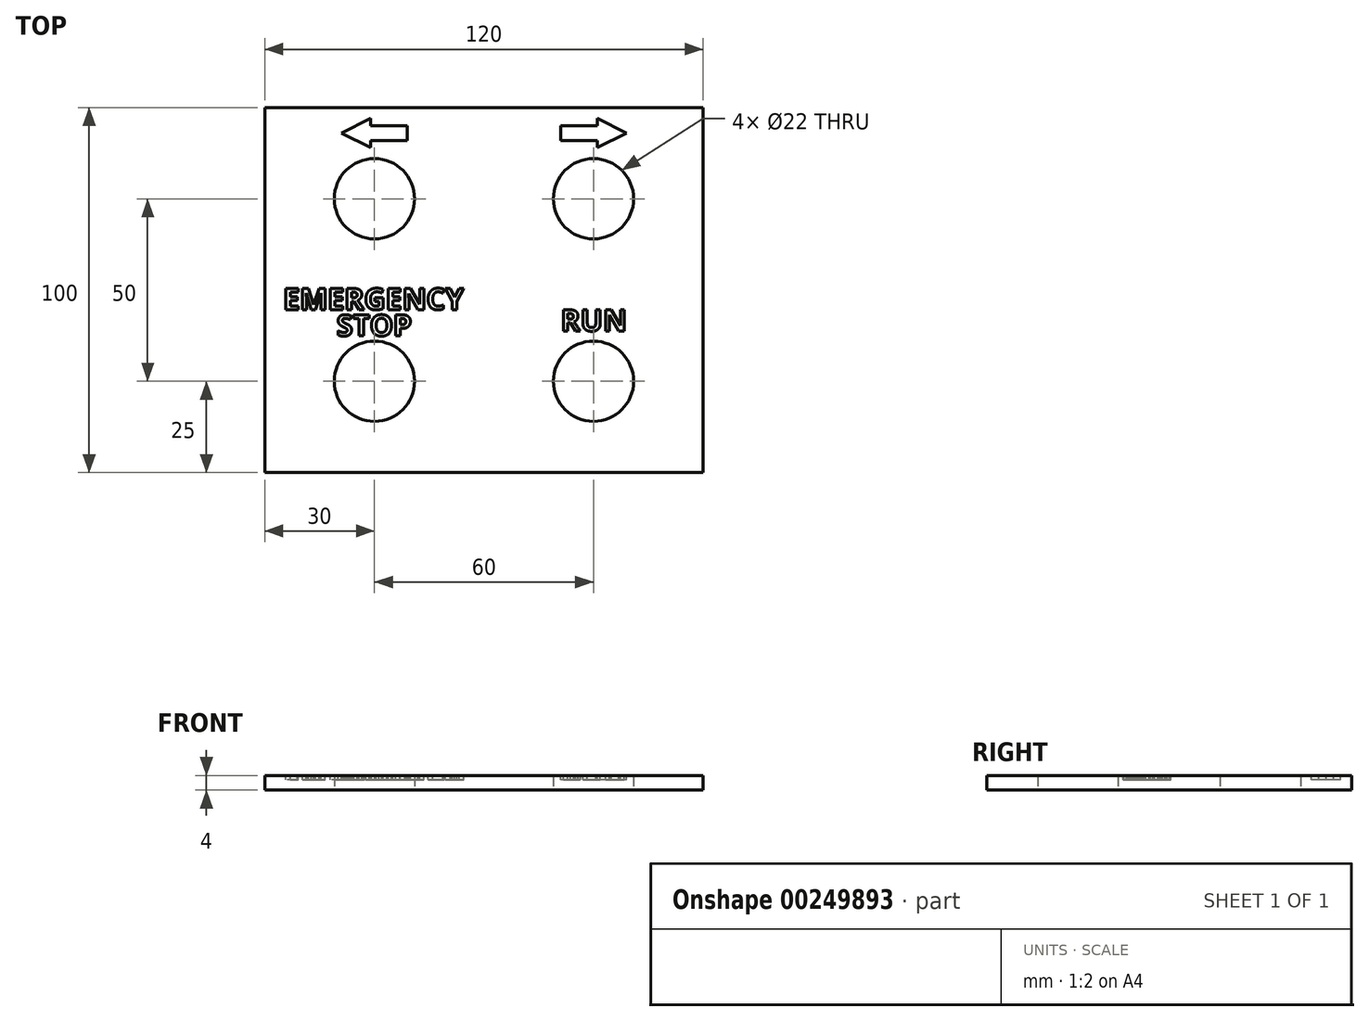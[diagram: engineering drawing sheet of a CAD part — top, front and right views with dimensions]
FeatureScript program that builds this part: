
annotation { "Feature Type Name" : "Feature", "Feature Type Description" : "" }
export const myFeature = defineFeature(function(context is Context, id is Id, definition is map)
    precondition{}
    {
        {
            var Q0;
            Q0=qCreatedBy(makeId("Top.planeOp"),FACE);
            var sketch = newSketch(context, id + "F0", { "sketchPlane" : qUnion([Q0])});
            skLineSegment(sketch, "E0.bottom", {"start": v(60, -50) * mm, "end": v(-60, -50) * mm});
            skLineSegment(sketch, "E0.top", {"start": v(60, 50) * mm, "end": v(-60, 50) * mm});
            skLineSegment(sketch, "E0.left", {"start": v(60, -50) * mm, "end": v(60, 50) * mm});
            skLineSegment(sketch, "E0.right", {"start": v(-60, -50) * mm, "end": v(-60, 50) * mm});
            skPoint(sketch, "E0.middle", {"position": v(0, 0) * mm});
            skCircle(sketch, "E1", {"center": v(-30, 25) * mm, "radius": 11 * mm});
            skLineSegment(sketch, "E2", {"start": v(0, -50) * mm, "end": v(0, 50) * mm, "construction": true});
            skLineSegment(sketch, "E3", {"start": v(-60, 0) * mm, "end": v(60, 0) * mm, "construction": true});
            skCircle(sketch, "E4.MirrorC", {"center": v(30, 25) * mm, "radius": 11 * mm});
            skCircle(sketch, "E5.MirrorC", {"center": v(30, -25) * mm, "radius": 11 * mm});
            skCircle(sketch, "E6.MirrorC", {"center": v(-30, -25) * mm, "radius": 11 * mm});
            skSolve(sketch);
        }
        {
            var Q0;
            Q0=makeQuery(id+"F0.imprint","IMPRINT",FACE,{"disambiguationData":[TD([[makeQuery(id+"F0.imprint","IMPRINT",EDGE,{"derivedFrom":sQuery(id+"F0.wireOp",EDGE,"E0.bottom")}),-1.0]])]});
            extrude(context, id + "F1", {"entities" : qUnion([Q0]), "depth" : 4 * mm});
        }
        {
            var Q0;
            Q0=makeQuery(id+"F1.opExtrude","CAP_FACE",FACE,{"disambiguationData":[OSD([sQuery(id+"F0.wireOp",EDGE,"E0.bottom"),sQuery(id+"F0.wireOp",EDGE,"E0.top"),sQuery(id+"F0.wireOp",EDGE,"E0.left"),sQuery(id+"F0.wireOp",EDGE,"E0.right"),sQuery(id+"F0.wireOp",EDGE,"E1"),sQuery(id+"F0.wireOp",EDGE,"E4.MirrorC"),sQuery(id+"F0.wireOp",EDGE,"E5.MirrorC"),sQuery(id+"F0.wireOp",EDGE,"E6.MirrorC")])],"isStart":false});
            var sketch = newSketch(context, id + "F2", { "sketchPlane" : qUnion([Q0])});
            skLineSegment(sketch, "E7", {"start": v(-31, 47) * mm, "end": v(-31, 39) * mm});
            skLineSegment(sketch, "E8", {"start": v(-31, 47) * mm, "end": v(-39, 43) * mm});
            skLineSegment(sketch, "E9", {"start": v(-39, 43) * mm, "end": v(-31, 39) * mm});
            skLineSegment(sketch, "E10.bottom", {"start": v(-31, 45) * mm, "end": v(-21, 45) * mm});
            skLineSegment(sketch, "E10.top", {"start": v(-31, 41) * mm, "end": v(-21, 41) * mm});
            skLineSegment(sketch, "E10.left", {"start": v(-31, 45) * mm, "end": v(-31, 41) * mm});
            skLineSegment(sketch, "E10.right", {"start": v(-21, 45) * mm, "end": v(-21, 41) * mm});
            skLineSegment(sketch, "E11", {"start": v(-21, 43) * mm, "end": v(-39, 43) * mm, "construction": true});
            skLineSegment(sketch, "E12", {"start": v(-30, 25) * mm, "end": v(-30, 41) * mm, "construction": true});
            skLineSegment(sketch, "E13.MirrorCS", {"start": v(31, 47) * mm, "end": v(39, 43) * mm});
            skLineSegment(sketch, "E14.MirrorCS", {"start": v(39, 43) * mm, "end": v(31, 39) * mm});
            skLineSegment(sketch, "E15.MirrorCS", {"start": v(31, 47) * mm, "end": v(31, 39) * mm});
            skLineSegment(sketch, "E16.MirrorCS", {"start": v(31, 45) * mm, "end": v(21, 45) * mm});
            skLineSegment(sketch, "E17.MirrorCS", {"start": v(31, 41) * mm, "end": v(21, 41) * mm});
            skLineSegment(sketch, "E18.MirrorCS", {"start": v(21, 45) * mm, "end": v(21, 41) * mm});
            skText(sketch, "E19", { "text": "EMERGENCY", "fontName": "OpenSans-Bold.ttf"});
            skText(sketch, "E20", { "text": "STOP", "fontName": "OpenSans-Bold.ttf"});
            skText(sketch, "E21", { "text": "RUN", "fontName": "OpenSans-Bold.ttf"});
            skLineSegment(sketch, "E22", {"start": v(30, -25) * mm, "end": v(30, 26.9) * mm, "construction": true});
            skLineSegment(sketch, "E23", {"start": v(-30, -25) * mm, "end": v(-30, 23.33) * mm, "construction": true});
            skLineSegment(sketch, "E24.bottom", {"start": v(60, 50) * mm, "end": v(-60, 50) * mm});
            skLineSegment(sketch, "E24.top", {"start": v(60, -50) * mm, "end": v(-60, -50) * mm});
            skLineSegment(sketch, "E24.left", {"start": v(60, 50) * mm, "end": v(60, -50) * mm});
            skLineSegment(sketch, "E24.right", {"start": v(-60, 50) * mm, "end": v(-60, -50) * mm});
            skPoint(sketch, "E24.middle", {"position": v(0, 0) * mm});
            const initialGuessF2  = {"E19": [-0.055, -0.00537, 1, 0, 0.00586], "E20": [-0.04037, -0.01258, 1, 0, 0.0058], "E21": [0.021, -0.01125, 1, 0, 0.00588]};
            skSetInitialGuess(sketch, initialGuessF2);
            skSolve(sketch);
        }
        {
            var Q0;
            {var subQ1=sQuery(id+"F2.wireOp",EDGE,"E8");Q0=makeQuery(id+"F2.imprint","IMPRINT",FACE,{"disambiguationData":[TD([[makeQuery(id+"F2.imprint","IMPRINT",EDGE,{"derivedFrom":subQ1}),1.0]])]});}
            var Q1;
            Q1=makeQuery(id+"F2.imprint","IMPRINT",FACE,{"disambiguationData":[TD([[makeQuery(id+"F2.imprint","IMPRINT",EDGE,{"derivedFrom":sQuery(id+"F2.wireOp",EDGE,"E10.bottom")}),-1.0]])]});
            var Q2;
            {var subQ0=sQuery(id+"F2.wireOp",EDGE,"E16.MirrorCS");Q2=makeQuery(id+"F2.imprint","IMPRINT",FACE,{"disambiguationData":[TD([[makeQuery(id+"F2.imprint","IMPRINT",EDGE,{"derivedFrom":subQ0}),1.0]])]});}
            var Q3;
            {var subQ3=sQuery(id+"F2.wireOp",EDGE,"E13.MirrorCS");Q3=makeQuery(id+"F2.imprint","IMPRINT",FACE,{"disambiguationData":[TD([[makeQuery(id+"F2.imprint","IMPRINT",EDGE,{"derivedFrom":subQ3}),-1.0]])]});}
            var Q4;
            Q4=makeQuery(id+"F2.imprint","IMPRINT",FACE,{"disambiguationData":[TD([[makeQuery(id+"F2.imprint","IMPRINT",EDGE,{"derivedFrom":sQuery(id+"F2.wireOp",EDGE,"E19.sketch_text.stroke-0")}),-1.0]])]});
            var Q5;
            Q5=makeQuery(id+"F2.imprint","IMPRINT",FACE,{"disambiguationData":[TD([[makeQuery(id+"F2.imprint","IMPRINT",EDGE,{"derivedFrom":sQuery(id+"F2.wireOp",EDGE,"E19.sketch_text.stroke-12")}),-1.0]])]});
            var Q6;
            Q6=makeQuery(id+"F2.imprint","IMPRINT",FACE,{"disambiguationData":[TD([[makeQuery(id+"F2.imprint","IMPRINT",EDGE,{"derivedFrom":sQuery(id+"F2.wireOp",EDGE,"E19.sketch_text.stroke-31")}),-1.0]])]});
            var Q7;
            Q7=makeQuery(id+"F2.imprint","IMPRINT",FACE,{"disambiguationData":[TD([[makeQuery(id+"F2.imprint","IMPRINT",EDGE,{"derivedFrom":sQuery(id+"F2.wireOp",EDGE,"E19.sketch_text.stroke-43")}),-1.0]])]});
            var Q8;
            Q8=makeQuery(id+"F2.imprint","IMPRINT",FACE,{"disambiguationData":[TD([[makeQuery(id+"F2.imprint","IMPRINT",EDGE,{"derivedFrom":sQuery(id+"F2.wireOp",EDGE,"E20.sketch_text.stroke-0")}),-1.0]])]});
            var Q9;
            Q9=makeQuery(id+"F2.imprint","IMPRINT",FACE,{"disambiguationData":[TD([[makeQuery(id+"F2.imprint","IMPRINT",EDGE,{"derivedFrom":sQuery(id+"F2.wireOp",EDGE,"E20.sketch_text.stroke-28")}),-1.0]])]});
            var Q10;
            Q10=makeQuery(id+"F2.imprint","IMPRINT",FACE,{"disambiguationData":[TD([[makeQuery(id+"F2.imprint","IMPRINT",EDGE,{"derivedFrom":sQuery(id+"F2.wireOp",EDGE,"E20.sketch_text.stroke-36")}),-1.0]])]});
            var Q11;
            Q11=makeQuery(id+"F2.imprint","IMPRINT",FACE,{"disambiguationData":[TD([[makeQuery(id+"F2.imprint","IMPRINT",EDGE,{"derivedFrom":sQuery(id+"F2.wireOp",EDGE,"E19.sketch_text.stroke-62")}),-1.0]])]});
            var Q12;
            Q12=makeQuery(id+"F2.imprint","IMPRINT",FACE,{"disambiguationData":[TD([[makeQuery(id+"F2.imprint","IMPRINT",EDGE,{"derivedFrom":sQuery(id+"F2.wireOp",EDGE,"E19.sketch_text.stroke-81")}),-1.0]])]});
            var Q13;
            Q13=makeQuery(id+"F2.imprint","IMPRINT",FACE,{"disambiguationData":[TD([[makeQuery(id+"F2.imprint","IMPRINT",EDGE,{"derivedFrom":sQuery(id+"F2.wireOp",EDGE,"E20.sketch_text.stroke-50")}),-1.0]])]});
            var Q14;
            Q14=makeQuery(id+"F2.imprint","IMPRINT",FACE,{"disambiguationData":[TD([[makeQuery(id+"F2.imprint","IMPRINT",EDGE,{"derivedFrom":sQuery(id+"F2.wireOp",EDGE,"E19.sketch_text.stroke-93")}),-1.0]])]});
            var Q15;
            Q15=makeQuery(id+"F2.imprint","IMPRINT",FACE,{"disambiguationData":[TD([[makeQuery(id+"F2.imprint","IMPRINT",EDGE,{"derivedFrom":sQuery(id+"F2.wireOp",EDGE,"E19.sketch_text.stroke-107")}),-1.0]])]});
            var Q16;
            Q16=makeQuery(id+"F2.imprint","IMPRINT",FACE,{"disambiguationData":[TD([[makeQuery(id+"F2.imprint","IMPRINT",EDGE,{"derivedFrom":sQuery(id+"F2.wireOp",EDGE,"E19.sketch_text.stroke-122")}),-1.0]])]});
            var Q17;
            Q17=makeQuery(id+"F2.imprint","IMPRINT",FACE,{"disambiguationData":[TD([[makeQuery(id+"F2.imprint","IMPRINT",EDGE,{"derivedFrom":sQuery(id+"F2.wireOp",EDGE,"E21.sketch_text.stroke-0")}),-1.0]])]});
            var Q18;
            Q18=makeQuery(id+"F2.imprint","IMPRINT",FACE,{"disambiguationData":[TD([[makeQuery(id+"F2.imprint","IMPRINT",EDGE,{"derivedFrom":sQuery(id+"F2.wireOp",EDGE,"E21.sketch_text.stroke-19")}),-1.0]])]});
            var Q19;
            Q19=makeQuery(id+"F2.imprint","IMPRINT",FACE,{"disambiguationData":[TD([[makeQuery(id+"F2.imprint","IMPRINT",EDGE,{"derivedFrom":sQuery(id+"F2.wireOp",EDGE,"E21.sketch_text.stroke-34")}),-1.0]])]});
            extrude(context, id + "F3", {"entities" : qUnion([Q0, Q1, Q2, Q3, Q4, Q5, Q6, Q7, Q8, Q9, Q10, Q11, Q12, Q13, Q14, Q15, Q16, Q17, Q18, Q19]), "operationType" : NewBodyOperationType.REMOVE, "oppositeDirection" : true, "depth" : 1.2 * mm});
        }
    });
